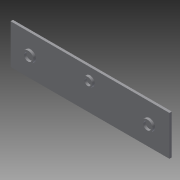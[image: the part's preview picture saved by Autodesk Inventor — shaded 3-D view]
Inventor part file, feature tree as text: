
AUTODESK INVENTOR PART (.ipt)
format: ipt  version: 2014 SP1 (Build 180222100, 222)  size: 122,368 bytes
history: native  units: mm
features: extrude x4, sketch x4
ambient origin geometry x8: Origin, YZ Plane, XZ Plane, XY Plane, X Axis, Y Axis, Z Axis, Center Point
bodies: Solid1 (feature_tree)
feature tree (8):
  extrude  "Extrusion1"  Depth=50.0mm
  extrude  "Extrusion2"  Depth=25.0mm
  extrude  "Extrusion3"  Depth=3.0mm TaperAngle=0.0deg
  extrude  "Extrusion4"  Depth=3.0mm
  sketch  "Sketch1"  dims[d0=200.0mm d1=50.0mm]
  sketch  "Sketch2"  dims[d2=75.0mm d3=25.0mm]
  sketch  "Sketch3"  dims[d4=15.0mm d5=3.0mm d6=0.0mm]
  sketch  "Sketch4"  dims[d7=15.0mm d8=25.0mm d9=75.0mm d10=75.0mm d11=8.0mm d12=12.0mm d13=3.0mm d14=0.0mm d15=75.0mm d16=25.0mm d17=10.0mm d18=14.0mm d19=3.0mm d20=0.0mm d21=75.0mm d22=25.0mm d23=10.0mm d24=14.0mm d25=3.0mm d26=0.0mm]
